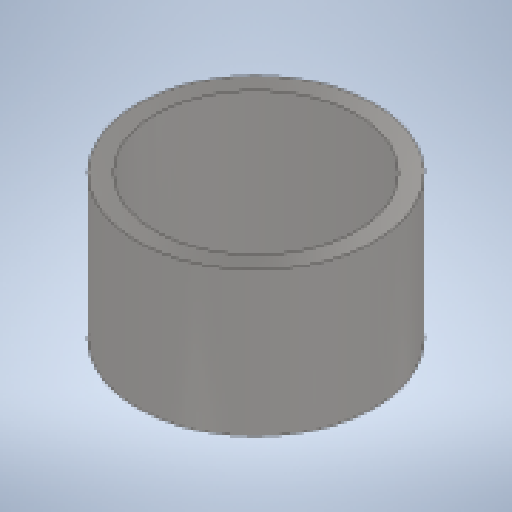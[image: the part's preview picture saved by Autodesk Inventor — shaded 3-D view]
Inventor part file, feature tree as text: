
AUTODESK INVENTOR PART (.ipt)
format: ipt  version: 2023.1 (Build 271208000, 208)  size: 242,176 bytes
history: native  units: in
note: dims shown in document units (in); Inventor stores cm internally (conversion verified against a paired STEP export)
features: extrude x1, sketch x1
ambient origin geometry x8: Origin, YZ Plane, XZ Plane, XY Plane, X Axis, Y Axis, Z Axis, Center Point
bodies: Solid1 (feature_tree)
feature tree (2):
  extrude  "Extrusion1"  Depth=0.315in TaperAngle=0.0deg
  sketch  "Sketch1"  dims[d0=0.0394in d1=0.315in d2=0.0in d3=0.6693in]
